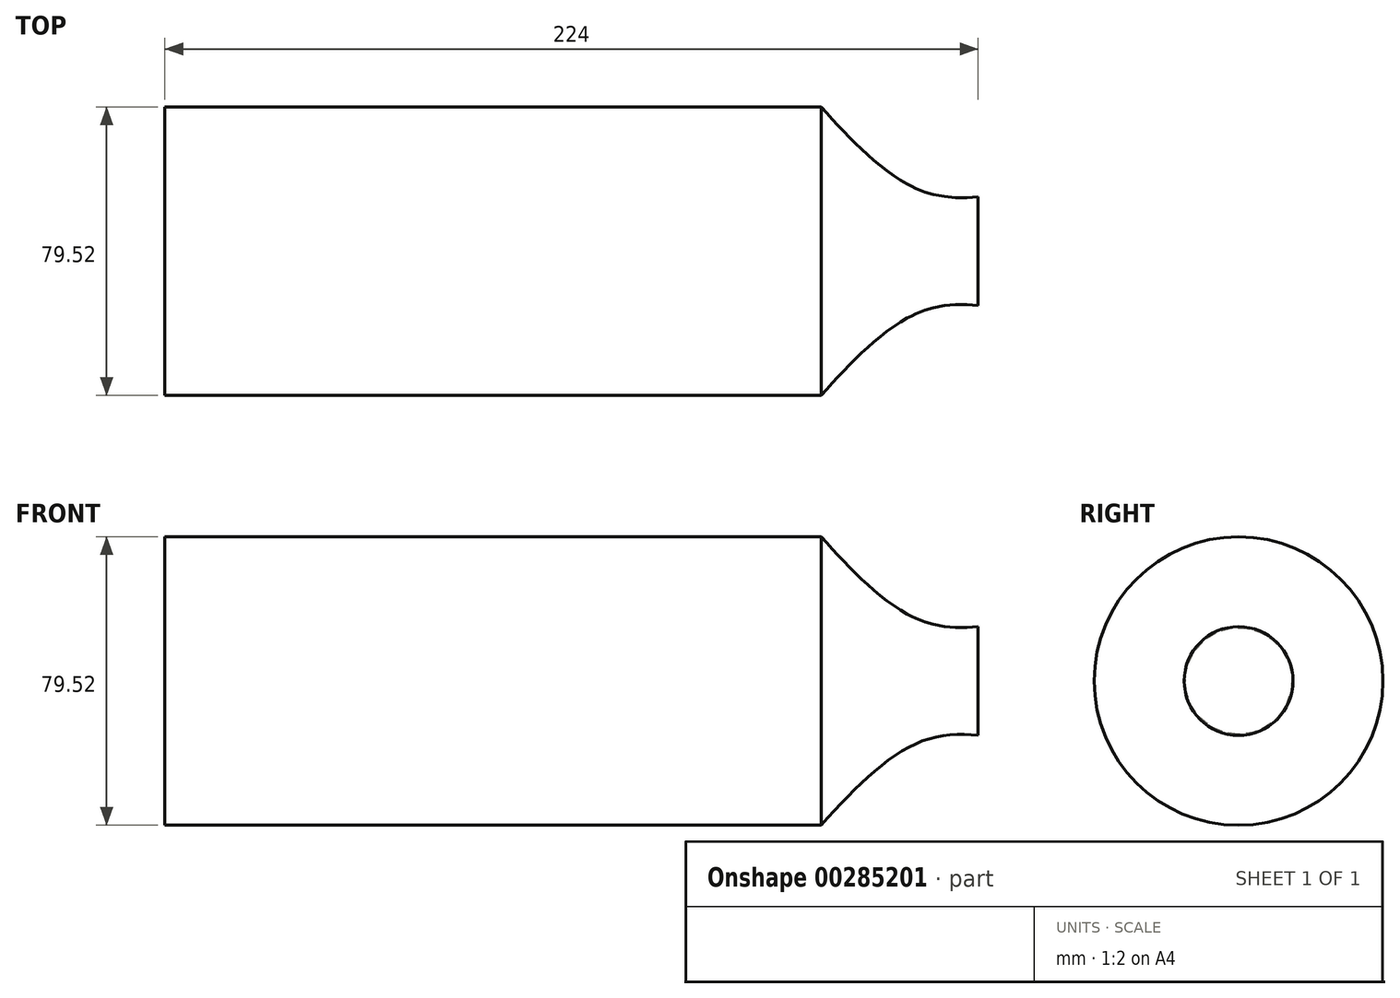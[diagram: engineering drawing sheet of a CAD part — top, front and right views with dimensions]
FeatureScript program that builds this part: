
annotation { "Feature Type Name" : "Feature", "Feature Type Description" : "" }
export const myFeature = defineFeature(function(context is Context, id is Id, definition is map)
    precondition{}
    {
        {
            var Q0;
            Q0=qCreatedBy(makeId("Right.planeOp"),FACE);
            var sketch = newSketch(context, id + "F0", { "sketchPlane" : qUnion([Q0])});
            skCircle(sketch, "E0", {"center": v(0, 0) * mm, "radius": 39.76 * mm});
            skSolve(sketch);
        }
        {
            var Q0;
            Q0 = qSketchRegion(id + "F0", true);
            extrude(context, id + "F1", {"entities" : qUnion([Q0]), "endBound" : BoundingType.SYMMETRIC, "oppositeDirection" : true, "depth" : 224 * mm});
        }
        {
            var Q0;
            Q0=qCreatedBy(makeId("Top.planeOp"),FACE);
            var sketch = newSketch(context, id + "F2", { "sketchPlane" : qUnion([Q0])});
            skFitSpline(sketch, "E1", {"points": [v(122.3, 16.57) * mm, v(96.62, 16.57) * mm, v(64.88, 44.11) * mm], "startDerivative": vector(-58.95, -10.76) * mm, "endDerivative": vector(-56, 62.84) * mm});
            skLineSegment(sketch, "E2", {"start": v(64.88, 44.11) * mm, "end": v(122.3, 44.11) * mm});
            skLineSegment(sketch, "E3", {"start": v(122.3, 44.11) * mm, "end": v(122.3, 16.57) * mm});
            skLineSegment(sketch, "E4", {"start": v(0, 0) * mm, "end": v(131.63, 0) * mm});
            skSolve(sketch);
        }
        {
            var Q0;
            Q0 = qSketchRegion(id + "F2", true);
            var Q1;
            Q1=sQuery(id+"F2.wireOp",EDGE,"E4");
            revolve(context, id + "F3", {"operationType" : NewBodyOperationType.REMOVE, "entities" : qUnion([Q0]), "axis" : qUnion([Q1]), "revolveType" : RevolveType.FULL, "oppositeDirection" : true});
        }
    });
